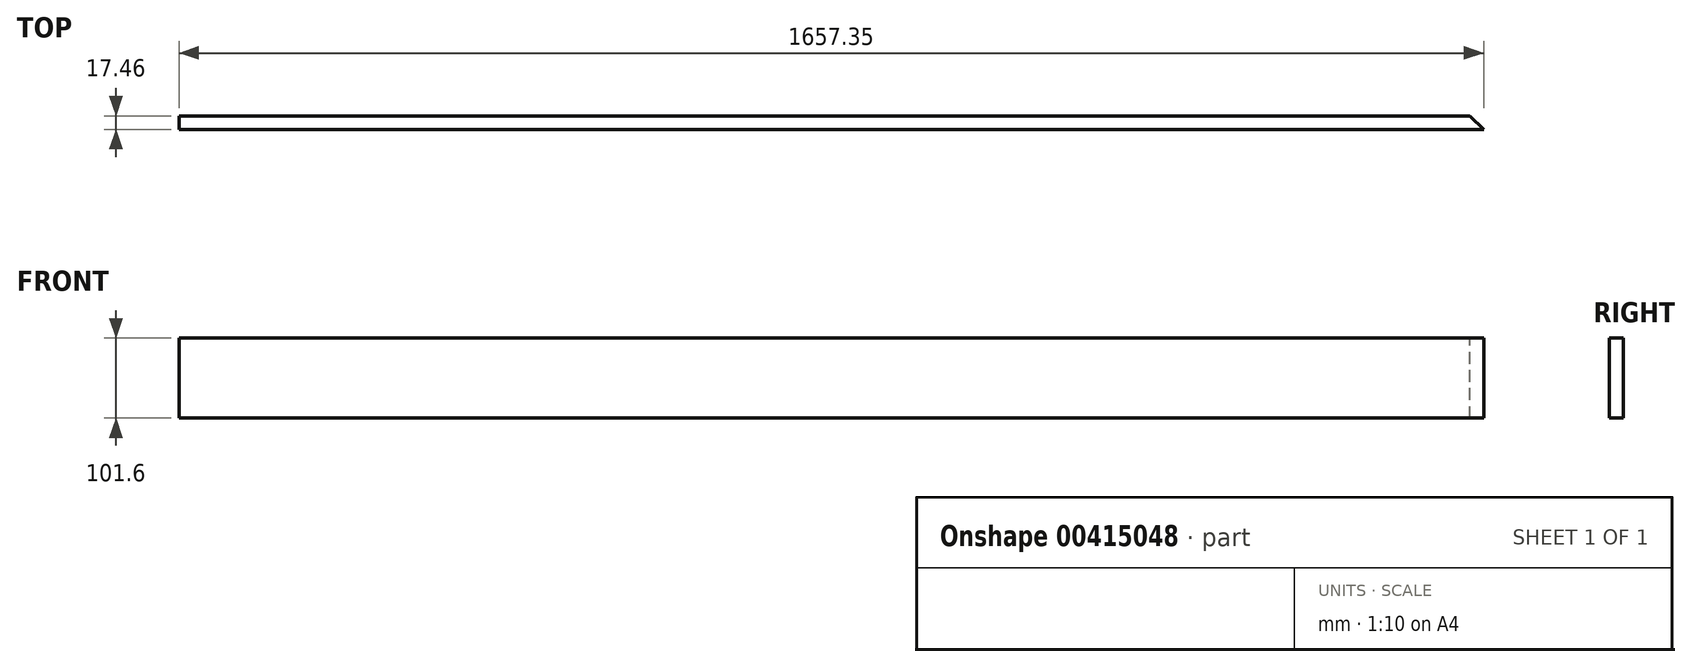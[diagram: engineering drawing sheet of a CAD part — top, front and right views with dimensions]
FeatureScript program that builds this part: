
annotation { "Feature Type Name" : "Feature", "Feature Type Description" : "" }
export const myFeature = defineFeature(function(context is Context, id is Id, definition is map)
    precondition{}
    {
        {
            var Q0;
            Q0=qCreatedBy(makeId("Front.planeOp"),FACE);
            var sketch = newSketch(context, id + "F0", { "sketchPlane" : qUnion([Q0])});
            skLineSegment(sketch, "E0.bottom", {"start": v(0, 0) * mm, "end": v(1905, 0) * mm});
            skLineSegment(sketch, "E0.top", {"start": v(0, 101.6) * mm, "end": v(1905, 101.6) * mm});
            skLineSegment(sketch, "E0.left", {"start": v(0, 0) * mm, "end": v(0, 101.6) * mm});
            skLineSegment(sketch, "E0.right", {"start": v(1905, 0) * mm, "end": v(1905, 101.6) * mm});
            skSolve(sketch);
        }
        {
            var Q0;
            Q0=makeQuery(id+"F0.imprint","IMPRINT",FACE,{"disambiguationData":[TD([[makeQuery(id+"F0.imprint","IMPRINT",EDGE,{"derivedFrom":sQuery(id+"F0.wireOp",EDGE,"E0.bottom")}),1.0]])]});
            extrude(context, id + "F1", {"entities" : qUnion([Q0]), "depth" : 17.46 * mm, "offsetDistance" : 25.4 * mm});
        }
        {
            var Q0;
            Q0=makeQuery(id+"F1.opExtrude","SWEPT_FACE",FACE,{"disambiguationData":[OSD([sQuery(id+"F0.wireOp",EDGE,"E0.top")])]});
            var sketch = newSketch(context, id + "F2", { "sketchPlane" : qUnion([Q0])});
            skLineSegment(sketch, "E1", {"start": v(1657.35, -17.46) * mm, "end": v(1639.89, 0) * mm});
            skSolve(sketch);
        }
        {
            var Q0;
            Q0 = qSketchRegion(id + "F2", true);
            var Q1;
            {var subQ0=sQuery(id+"F2.wireOp",EDGE,"E1");Q1=makeQuery(id+"F2.imprint","IMPRINT",FACE,{"disambiguationData":[TD([[makeQuery(id+"F2.imprint","IMPRINT",EDGE,{"derivedFrom":subQ0}),-1.0]])]});}
            extrude(context, id + "F3", {"entities" : qUnion([Q0, Q1]), "operationType" : NewBodyOperationType.REMOVE, "endBound" : BoundingType.THROUGH_ALL, "oppositeDirection" : true, "depth" : 25.4 * mm, "offsetDistance" : 25.4 * mm});
        }
    });
